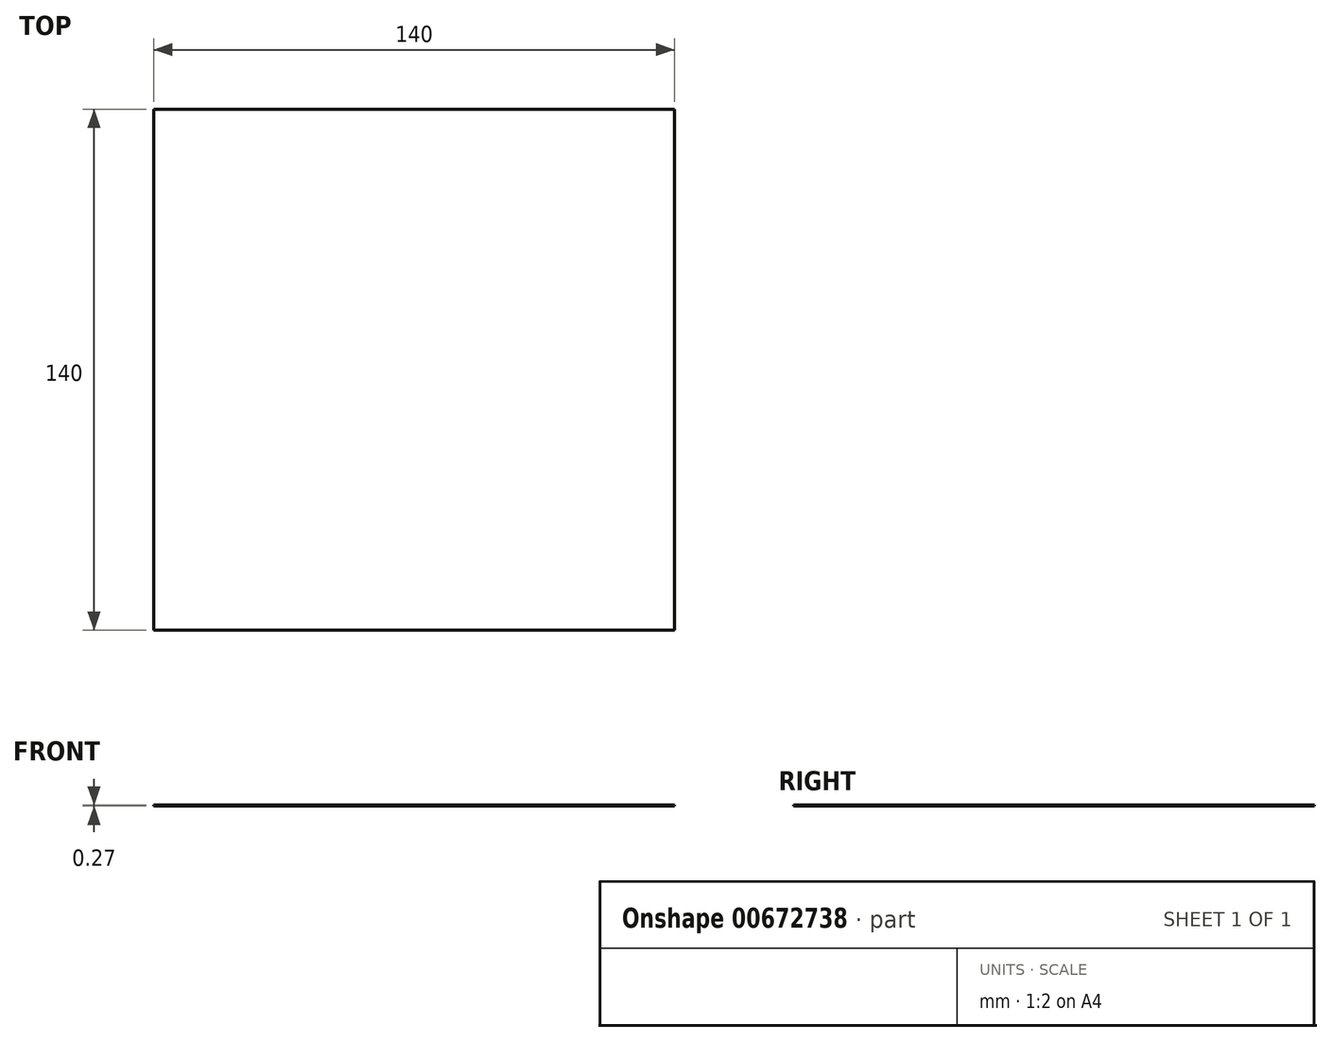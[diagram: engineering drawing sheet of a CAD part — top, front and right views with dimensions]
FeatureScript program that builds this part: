
annotation { "Feature Type Name" : "Feature", "Feature Type Description" : "" }
export const myFeature = defineFeature(function(context is Context, id is Id, definition is map)
    precondition{}
    {
        {
            var Q0;
            Q0=qCreatedBy(makeId("Top.planeOp"),FACE);
            var sketch = newSketch(context, id + "F0", { "sketchPlane" : qUnion([Q0])});
            skLineSegment(sketch, "E0.bottom", {"start": v(70, -70) * mm, "end": v(-70, -70) * mm});
            skLineSegment(sketch, "E0.top", {"start": v(70, 70) * mm, "end": v(-70, 70) * mm});
            skLineSegment(sketch, "E0.left", {"start": v(70, -70) * mm, "end": v(70, 70) * mm});
            skLineSegment(sketch, "E0.right", {"start": v(-70, -70) * mm, "end": v(-70, 70) * mm});
            skPoint(sketch, "E0.middle", {"position": v(0, 0) * mm});
            skSolve(sketch);
        }
        {
            var Q0;
            Q0 = qSketchRegion(id + "F0", true);
            extrude(context, id + "F1", {"entities" : qUnion([Q0]), "depth" : 0.27 * mm, "offsetDistance" : 25 * mm});
        }
    });
